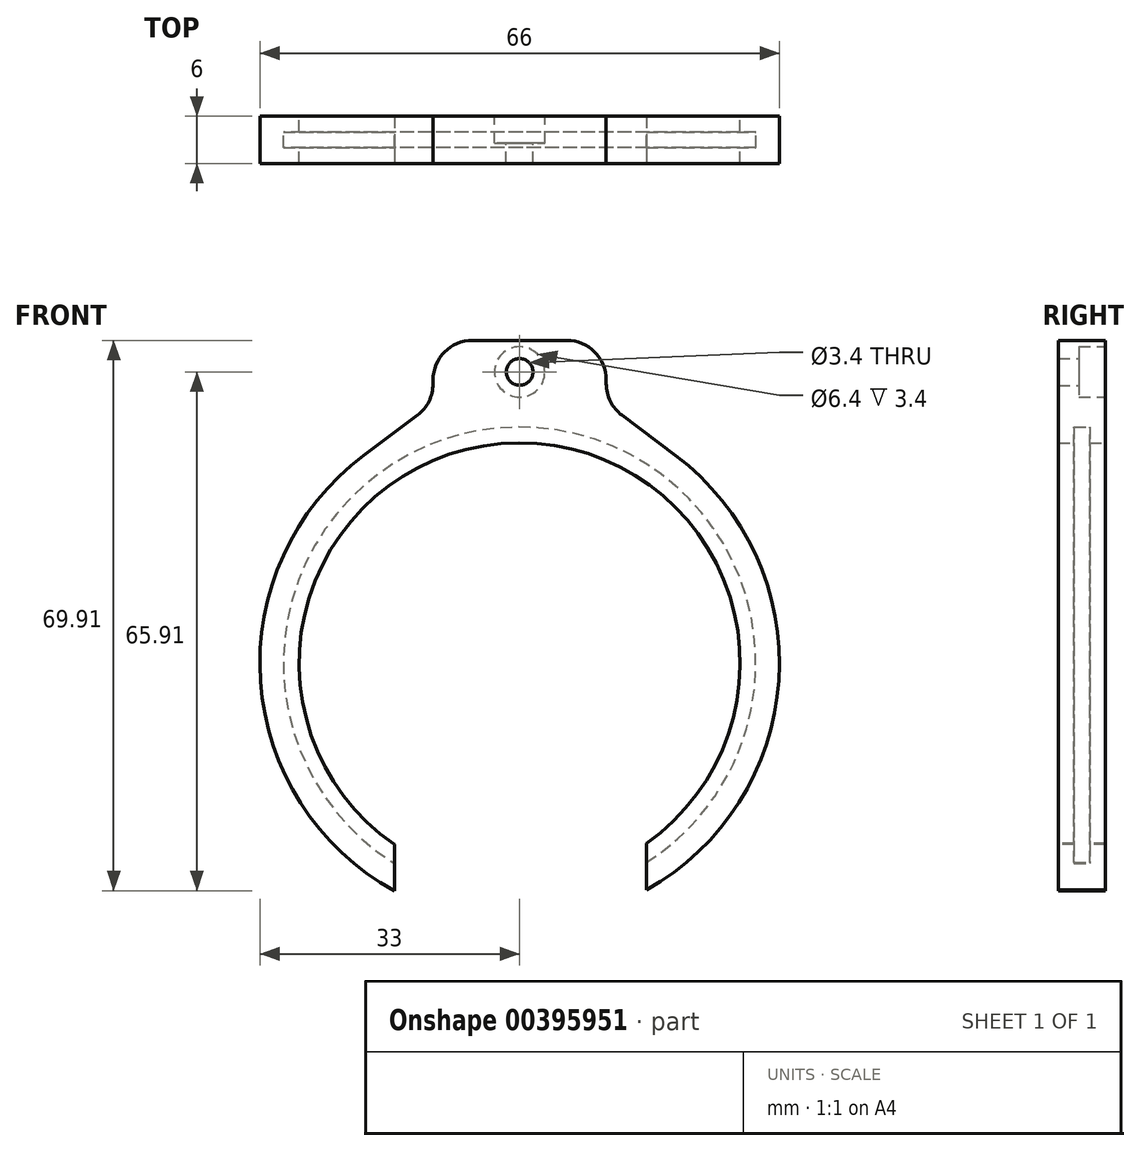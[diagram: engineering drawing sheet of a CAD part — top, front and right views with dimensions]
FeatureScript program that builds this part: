
annotation { "Feature Type Name" : "Feature", "Feature Type Description" : "" }
export const myFeature = defineFeature(function(context is Context, id is Id, definition is map)
    precondition{}
    {
        {
            var Q0;
            Q0=qCreatedBy(makeId("Front.planeOp"),FACE);
            var sketch = newSketch(context, id + "F0", { "sketchPlane" : qUnion([Q0])});
            skCircle(sketch, "E0", {"center": v(0, 0) * mm, "radius": 33 * mm});
            skCircle(sketch, "E1", {"center": v(0, 0) * mm, "radius": 28 * mm});
            skLineSegment(sketch, "E2.bottom", {"start": v(-11, 41) * mm, "end": v(0, 41) * mm});
            skLineSegment(sketch, "E2.top", {"start": v(-11, 33) * mm, "end": v(0, 33) * mm});
            skLineSegment(sketch, "E2.left", {"start": v(-11, 41) * mm, "end": v(-11, 35.5) * mm});
            skLineSegment(sketch, "E2.right", {"start": v(0, 41) * mm, "end": v(0, 33) * mm});
            skLineSegment(sketch, "E3.bottom", {"start": v(0, 41) * mm, "end": v(11, 41) * mm});
            skLineSegment(sketch, "E3.top", {"start": v(0, 33) * mm, "end": v(11, 33) * mm});
            skLineSegment(sketch, "E3.right", {"start": v(11, 41) * mm, "end": v(11, 35.5) * mm});
            skLineSegment(sketch, "E4", {"start": v(13, 31.5) * mm, "end": v(19.8, 26.4) * mm});
            skLineSegment(sketch, "E5", {"start": v(-13, 31.5) * mm, "end": v(-19.8, 26.4) * mm});
            skPoint(sketch, "E6.visualSharp", {"position": v(-11, 33) * mm});
            skArc(sketch, "E6.filletArc", {"start": v(-13, 31.5) * mm, "mid": v(-11.53, 33.26) * mm, "end": v(-11, 35.5) * mm});
            skPoint(sketch, "E7.visualSharp", {"position": v(11, 33) * mm});
            skArc(sketch, "E7.filletArc", {"start": v(11, 35.5) * mm, "mid": v(11.53, 33.26) * mm, "end": v(13, 31.5) * mm});
            skCircle(sketch, "E8", {"center": v(0, 37) * mm, "radius": 1.5 * mm});
            skSolve(sketch);
        }
        {
            var Q0;
            Q0=makeQuery(id+"F0.imprint","IMPRINT",FACE,{"disambiguationData":[TD([[makeQuery(id+"F0.imprint","IMPRINT",EDGE,{"derivedFrom":sQuery(id+"F0.wireOp",EDGE,"E1")}),-1.0]])]});
            var Q1;
            Q1=makeQuery(id+"F0.imprint","IMPRINT",FACE,{"disambiguationData":[TD([[makeQuery(id+"F0.imprint","IMPRINT",EDGE,{"derivedFrom":sQuery(id+"F0.wireOp",EDGE,"E2.bottom")}),-1.0]])]});
            var Q2;
            {var subQ0=sQuery(id+"F0.wireOp",EDGE,"E2.right");Q2=makeQuery(id+"F0.imprint","IMPRINT",FACE,{"disambiguationData":[TD([[makeQuery(id+"F0.imprint","IMPRINT",EDGE,{"derivedFrom":subQ0}),1.0]])]});}
            extrude(context, id + "F1", {"entities" : qUnion([Q0, Q1, Q2]), "depth" : 2 * mm});
        }
        {
            var Q0;
            Q0=makeQuery(id+"F1.opExtrude","CAP_FACE",FACE,{"disambiguationData":[OSD([sQuery(id+"F0.wireOp",EDGE,"E0"),sQuery(id+"F0.wireOp",EDGE,"E1"),sQuery(id+"F0.wireOp",EDGE,"E2.bottom"),sQuery(id+"F0.wireOp",EDGE,"E2.left"),sQuery(id+"F0.wireOp",EDGE,"E3.bottom"),sQuery(id+"F0.wireOp",EDGE,"E3.right"),sQuery(id+"F0.wireOp",EDGE,"E4"),sQuery(id+"F0.wireOp",EDGE,"E5"),sQuery(id+"F0.wireOp",EDGE,"E6.filletArc"),sQuery(id+"F0.wireOp",EDGE,"E7.filletArc")])],"isStart":false});
            var sketch = newSketch(context, id + "F2", { "sketchPlane" : qUnion([Q0])});
            skCircle(sketch, "E9", {"center": v(0, 0) * mm, "radius": 30 * mm});
            skSolve(sketch);
        }
        {
            var Q0;
            Q0=makeQuery(id+"F2.imprint","IMPRINT",FACE,{"disambiguationData":[TD([[makeQuery(id+"F2.imprint","IMPRINT",EDGE,{"derivedFrom":sQuery(id+"F2.wireOp",EDGE,"E9")}),-1.0]])]});
            extrude(context, id + "F3", {"entities" : qUnion([Q0]), "operationType" : NewBodyOperationType.ADD, "depth" : 2 * mm});
        }
        {
            var Q0;
            Q0=makeQuery(id+"F3.opExtrude","CAP_FACE",FACE,{"disambiguationData":[OSD([sQuery(id+"F0.wireOp",EDGE,"E0"),sQuery(id+"F0.wireOp",EDGE,"E2.bottom"),sQuery(id+"F0.wireOp",EDGE,"E2.left"),sQuery(id+"F0.wireOp",EDGE,"E3.bottom"),sQuery(id+"F0.wireOp",EDGE,"E3.right"),sQuery(id+"F0.wireOp",EDGE,"E4"),sQuery(id+"F0.wireOp",EDGE,"E5"),sQuery(id+"F0.wireOp",EDGE,"E6.filletArc"),sQuery(id+"F0.wireOp",EDGE,"E7.filletArc"),sQuery(id+"F2.wireOp",EDGE,"E9")])],"isStart":false});
            var sketch = newSketch(context, id + "F4", { "sketchPlane" : qUnion([Q0])});
            skCircle(sketch, "E10", {"center": v(0, 0) * mm, "radius": 28 * mm});
            skCircle(sketch, "E11", {"center": v(0, 0) * mm, "radius": 33 * mm});
            skSolve(sketch);
        }
        {
            var Q0;
            Q0=makeQuery(id+"F4.imprint","IMPRINT",FACE,{"disambiguationData":[TD([[makeQuery(id+"F4.imprint","IMPRINT",EDGE,{"derivedFrom":makeQuery(id+"F3.opExtrude","CAP_EDGE",EDGE,{"disambiguationData":[OSD([sQuery(id+"F2.wireOp",EDGE,"E9")])],"isStart":false})}),-1.0]])]});
            var Q1;
            Q1=makeQuery(id+"F4.imprint","IMPRINT",FACE,{"disambiguationData":[TD([[makeQuery(id+"F4.imprint","IMPRINT",EDGE,{"derivedFrom":sQuery(id+"F4.wireOp",EDGE,"E10")}),-1.0]])]});
            extrude(context, id + "F5", {"entities" : qUnion([Q0, Q1]), "operationType" : NewBodyOperationType.ADD, "depth" : 2 * mm});
        }
        {
            var Q0;
            Q0=makeQuery(id+"F3.opExtrude","CAP_FACE",FACE,{"disambiguationData":[OSD([sQuery(id+"F0.wireOp",EDGE,"E0"),sQuery(id+"F0.wireOp",EDGE,"E2.bottom"),sQuery(id+"F0.wireOp",EDGE,"E2.left"),sQuery(id+"F0.wireOp",EDGE,"E3.bottom"),sQuery(id+"F0.wireOp",EDGE,"E3.right"),sQuery(id+"F0.wireOp",EDGE,"E4"),sQuery(id+"F0.wireOp",EDGE,"E5"),sQuery(id+"F0.wireOp",EDGE,"E6.filletArc"),sQuery(id+"F0.wireOp",EDGE,"E7.filletArc"),sQuery(id+"F2.wireOp",EDGE,"E9")])],"isStart":false});
            extrude(context, id + "F6", {"entities" : qUnion([Q0]), "operationType" : NewBodyOperationType.ADD, "depth" : 2 * mm});
        }
        {
            var Q0;
            {var subQ0=sQuery(id+"F0.wireOp",EDGE,"E3.bottom");var subQ1=sQuery(id+"F0.wireOp",EDGE,"E2.left");var subQ2=sQuery(id+"F0.wireOp",EDGE,"E2.bottom");Q0=makeQuery(id+"F6.boolean.opBoolean","MERGE",EDGE,{"derivedFrom":[makeQuery(id+"F3.boolean.opBoolean","MERGE",EDGE,{"derivedFrom":[makeQuery(id+"F1.opExtrude","SWEPT_EDGE",EDGE,{"disambiguationData":[OSD([subQ2,subQ1])]}),makeQuery(id+"F3.opExtrude","SWEPT_EDGE",EDGE,{"disambiguationData":[OSD([subQ2,subQ1,subQ0])]})]}),makeQuery(id+"F6.opExtrude","SWEPT_EDGE",EDGE,{"disambiguationData":[OSD([subQ2,subQ1,subQ0])]})]});}
            fillet(context, id + "F7", {"entities" : qUnion([Q0]), "radius" : 5 * mm, "tangentPropagation" : true, "allowEdgeOverflow" : false});
        }
        {
            var Q0;
            {var subQ0=sQuery(id+"F0.wireOp",EDGE,"E3.right");var subQ1=sQuery(id+"F0.wireOp",EDGE,"E3.bottom");var subQ2=sQuery(id+"F0.wireOp",EDGE,"E2.bottom");Q0=makeQuery(id+"F6.boolean.opBoolean","MERGE",EDGE,{"derivedFrom":[makeQuery(id+"F3.boolean.opBoolean","MERGE",EDGE,{"derivedFrom":[makeQuery(id+"F1.opExtrude","SWEPT_EDGE",EDGE,{"disambiguationData":[OSD([subQ1,subQ0])]}),makeQuery(id+"F3.opExtrude","SWEPT_EDGE",EDGE,{"disambiguationData":[OSD([subQ2,subQ1,subQ0])]})]}),makeQuery(id+"F6.opExtrude","SWEPT_EDGE",EDGE,{"disambiguationData":[OSD([subQ2,subQ1,subQ0])]})]});}
            fillet(context, id + "F8", {"entities" : qUnion([Q0]), "radius" : 5 * mm, "tangentPropagation" : true, "allowEdgeOverflow" : false});
        }
        {
            var Q0;
            Q0=makeQuery(id+"F6.boolean.opBoolean","MERGE",FACE,{"derivedFrom":[makeQuery(id+"F5.opExtrude","CAP_FACE",FACE,{"disambiguationData":[OSD([sQuery(id+"F4.wireOp",EDGE,"E10"),sQuery(id+"F4.wireOp",EDGE,"E11")])],"isStart":false}),makeQuery(id+"F6.opExtrude","CAP_FACE",FACE,{"disambiguationData":[OSD([sQuery(id+"F0.wireOp",EDGE,"E0"),sQuery(id+"F0.wireOp",EDGE,"E2.bottom"),sQuery(id+"F0.wireOp",EDGE,"E2.left"),sQuery(id+"F0.wireOp",EDGE,"E3.bottom"),sQuery(id+"F0.wireOp",EDGE,"E3.right"),sQuery(id+"F0.wireOp",EDGE,"E4"),sQuery(id+"F0.wireOp",EDGE,"E5"),sQuery(id+"F0.wireOp",EDGE,"E6.filletArc"),sQuery(id+"F0.wireOp",EDGE,"E7.filletArc"),sQuery(id+"F2.wireOp",EDGE,"E9")])],"isStart":false})]});
            var sketch = newSketch(context, id + "F9", { "sketchPlane" : qUnion([Q0])});
            skLineSegment(sketch, "E12.bottom", {"start": v(-15.92, -21.41) * mm, "end": v(16.08, -21.41) * mm});
            skLineSegment(sketch, "E12.top", {"start": v(-15.92, -34.54) * mm, "end": v(16.08, -34.54) * mm});
            skLineSegment(sketch, "E12.left", {"start": v(-15.92, -21.41) * mm, "end": v(-15.92, -34.54) * mm});
            skLineSegment(sketch, "E12.right", {"start": v(16.08, -21.41) * mm, "end": v(16.08, -34.54) * mm});
            skSolve(sketch);
        }
        {
            var Q0;
            {var subQ0=sQuery(id+"F9.wireOp",EDGE,"E12.left");var subQ1=makeQuery(id+"F5.opExtrude","CAP_EDGE",EDGE,{"disambiguationData":[OSD([sQuery(id+"F4.wireOp",EDGE,"E11")])],"isStart":false});var subQ2=makeQuery(id+"F9.imprint","INTERSECT",VERTEX,{"derivedFrom":[subQ1,subQ0]});Q0=makeQuery(id+"F9.imprint","IMPRINT",FACE,{"disambiguationData":[TD([[makeQuery(id+"F9.imprint","IMPRINT",EDGE,{"disambiguationData":[TD([[subQ2,1.0]])],"derivedFrom":subQ0}),1.0]])]});}
            extrude(context, id + "F10", {"entities" : qUnion([Q0]), "operationType" : NewBodyOperationType.REMOVE, "oppositeDirection" : true, "depth" : 6 * mm});
        }
        {
            var Q0;
            Q0=sQuery(id+"F0.wireOp",VERTEX,"E8.center");
            var Q1;
            Q1=makeQuery(id+"F1.opExtrude","SWEPT_BODY",BODY,{"disambiguationData":[OSD([sQuery(id+"F0.wireOp",EDGE,"E0"),sQuery(id+"F0.wireOp",EDGE,"E1"),sQuery(id+"F0.wireOp",EDGE,"E2.bottom"),sQuery(id+"F0.wireOp",EDGE,"E2.left"),sQuery(id+"F0.wireOp",EDGE,"E3.bottom"),sQuery(id+"F0.wireOp",EDGE,"E3.right"),sQuery(id+"F0.wireOp",EDGE,"E4"),sQuery(id+"F0.wireOp",EDGE,"E5"),sQuery(id+"F0.wireOp",EDGE,"E6.filletArc"),sQuery(id+"F0.wireOp",EDGE,"E7.filletArc"),sQuery(id+"F0.wireOp",EDGE,"E8")])]});
            hole(context, id + "F11", {"style" : HoleStyle.C_BORE, "endStyle" : HoleEndStyle.THROUGH, "oppositeDirection" : true, "holeDiameter" : 3.4 * mm, "cBoreDiameter" : 6.4 * mm, "cBoreDepth" : 3.4 * mm, "isTappedThrough" : true, "tappedDepth" : 12 * mm, "tapClearance" : 3, "locations" : qUnion([Q0]), "scope" : qUnion([Q1])});
        }
    });
